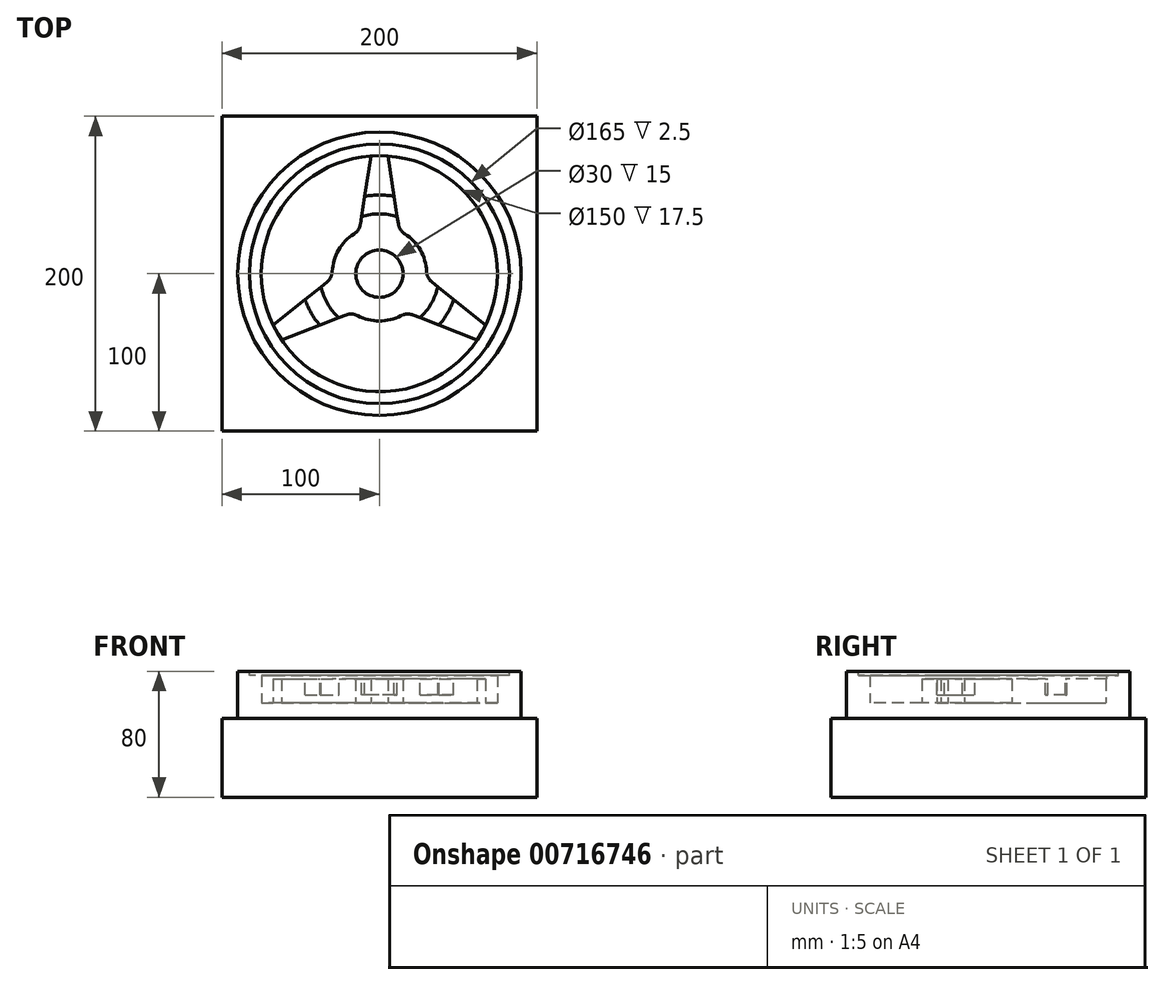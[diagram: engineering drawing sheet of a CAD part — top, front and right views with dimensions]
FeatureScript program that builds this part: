
annotation { "Feature Type Name" : "Feature", "Feature Type Description" : "" }
export const myFeature = defineFeature(function(context is Context, id is Id, definition is map)
    precondition{}
    {
        {
            var Q0;
            Q0=qCreatedBy(makeId("Top.planeOp"),FACE);
            var sketch = newSketch(context, id + "F0", { "sketchPlane" : qUnion([Q0])});
            skLineSegment(sketch, "E0.bottom", {"start": v(-100, 100) * mm, "end": v(100, 100) * mm});
            skLineSegment(sketch, "E0.top", {"start": v(-100, -100) * mm, "end": v(100, -100) * mm});
            skLineSegment(sketch, "E0.left", {"start": v(-100, 100) * mm, "end": v(-100, -100) * mm});
            skLineSegment(sketch, "E0.right", {"start": v(100, 100) * mm, "end": v(100, -100) * mm});
            skPoint(sketch, "E0.middle", {"position": v(0, 0) * mm});
            skCircle(sketch, "E1", {"center": v(0, 0) * mm, "radius": 90 * mm});
            skCircle(sketch, "E2", {"center": v(0, 0) * mm, "radius": 75 * mm});
            skCircle(sketch, "E3", {"center": v(0, 0) * mm, "radius": 30 * mm});
            skCircle(sketch, "E4", {"center": v(0, 0) * mm, "radius": 15 * mm});
            skLineSegment(sketch, "E5", {"start": v(0, 100) * mm, "end": v(0, -100) * mm, "construction": true});
            skLineSegment(sketch, "E6", {"start": v(-5.42, 74.8) * mm, "end": v(-12.73, 27.17) * mm});
            skLineSegment(sketch, "E7.MirrorCS", {"start": v(5.42, 74.8) * mm, "end": v(12.73, 27.17) * mm});
            skLineSegment(sketch, "E8.1.0", {"start": v(-67.5, -32.7) * mm, "end": v(-29.9, -2.56) * mm});
            skLineSegment(sketch, "E8.1.1", {"start": v(-62.07, -42.1) * mm, "end": v(-17.16, -24.6) * mm});
            skLineSegment(sketch, "E8.2.0", {"start": v(62.07, -42.1) * mm, "end": v(17.16, -24.6) * mm});
            skLineSegment(sketch, "E8.2.1", {"start": v(67.5, -32.7) * mm, "end": v(29.9, -2.56) * mm});
            skSolve(sketch);
        }
        {
            var Q0;
            Q0=makeQuery(id+"F0.imprint","IMPRINT",FACE,{"disambiguationData":[TD([[makeQuery(id+"F0.imprint","IMPRINT",EDGE,{"derivedFrom":sQuery(id+"F0.wireOp",EDGE,"E0.bottom")}),-1.0]])]});
            var Q1;
            Q1=makeQuery(id+"F0.imprint","IMPRINT",FACE,{"disambiguationData":[TD([[makeQuery(id+"F0.imprint","IMPRINT",EDGE,{"derivedFrom":sQuery(id+"F0.wireOp",EDGE,"E1")}),1.0]])]});
            var Q2;
            {var subQ0=sQuery(id+"F0.wireOp",EDGE,"E6");Q2=makeQuery(id+"F0.imprint","IMPRINT",FACE,{"disambiguationData":[TD([[makeQuery(id+"F0.imprint","IMPRINT",EDGE,{"derivedFrom":subQ0}),-1.0]])]});}
            var Q3;
            {var subQ0=sQuery(id+"F0.wireOp",EDGE,"fdc0faed-76a0-460e-8b43-f14472de8eec.1.0");Q3=makeQuery(id+"F0.imprint","IMPRINT",FACE,{"disambiguationData":[TD([[makeQuery(id+"F0.imprint","IMPRINT",EDGE,{"derivedFrom":subQ0}),-1.0]])]});}
            var Q4;
            {var subQ0=sQuery(id+"F0.wireOp",EDGE,"fdc0faed-76a0-460e-8b43-f14472de8eec.1.1");Q4=makeQuery(id+"F0.imprint","IMPRINT",FACE,{"disambiguationData":[TD([[makeQuery(id+"F0.imprint","IMPRINT",EDGE,{"derivedFrom":subQ0}),-1.0]])]});}
            var Q5;
            {var subQ0=sQuery(id+"F0.wireOp",EDGE,"fdc0faed-76a0-460e-8b43-f14472de8eec.2.0");Q5=makeQuery(id+"F0.imprint","IMPRINT",FACE,{"disambiguationData":[TD([[makeQuery(id+"F0.imprint","IMPRINT",EDGE,{"derivedFrom":subQ0}),-1.0]])]});}
            var Q6;
            Q6=makeQuery(id+"F0.imprint","IMPRINT",FACE,{"disambiguationData":[TD([[makeQuery(id+"F0.imprint","IMPRINT",EDGE,{"derivedFrom":sQuery(id+"F0.wireOp",EDGE,"E4")}),-1.0]])]});
            var Q7;
            Q7=makeQuery(id+"F0.imprint","IMPRINT",FACE,{"disambiguationData":[TD([[makeQuery(id+"F0.imprint","IMPRINT",EDGE,{"derivedFrom":sQuery(id+"F0.wireOp",EDGE,"E4")}),1.0]])]});
            var Q8;
            {var subQ0=sQuery(id+"F0.wireOp",EDGE,"fdc0faed-76a0-460e-8b43-f14472de8eec.3.0");Q8=makeQuery(id+"F0.imprint","IMPRINT",FACE,{"disambiguationData":[TD([[makeQuery(id+"F0.imprint","IMPRINT",EDGE,{"derivedFrom":subQ0}),-1.0]])]});}
            var Q9;
            {var subQ0=sQuery(id+"F0.wireOp",EDGE,"fdc0faed-76a0-460e-8b43-f14472de8eec.3.1");Q9=makeQuery(id+"F0.imprint","IMPRINT",FACE,{"disambiguationData":[TD([[makeQuery(id+"F0.imprint","IMPRINT",EDGE,{"derivedFrom":subQ0}),-1.0]])]});}
            var Q10;
            {var subQ0=sQuery(id+"F0.wireOp",EDGE,"E7.MirrorCS");Q10=makeQuery(id+"F0.imprint","IMPRINT",FACE,{"disambiguationData":[TD([[makeQuery(id+"F0.imprint","IMPRINT",EDGE,{"derivedFrom":subQ0}),1.0]])]});}
            var Q11;
            {var subQ0=sQuery(id+"F0.wireOp",EDGE,"fdc0faed-76a0-460e-8b43-f14472de8eec.4.0");Q11=makeQuery(id+"F0.imprint","IMPRINT",FACE,{"disambiguationData":[TD([[makeQuery(id+"F0.imprint","IMPRINT",EDGE,{"derivedFrom":subQ0}),-1.0]])]});}
            var Q12;
            {var subQ0=sQuery(id+"F0.wireOp",EDGE,"E6");Q12=makeQuery(id+"F0.imprint","IMPRINT",FACE,{"disambiguationData":[TD([[makeQuery(id+"F0.imprint","IMPRINT",EDGE,{"derivedFrom":subQ0}),1.0]])]});}
            var Q13;
            {var subQ0=sQuery(id+"F0.wireOp",EDGE,"fdc0faed-76a0-460e-8b43-f14472de8eec.2.1");Q13=makeQuery(id+"F0.imprint","IMPRINT",FACE,{"disambiguationData":[TD([[makeQuery(id+"F0.imprint","IMPRINT",EDGE,{"derivedFrom":subQ0}),-1.0]])]});}
            var Q14;
            {var subQ0=sQuery(id+"F0.wireOp",EDGE,"E8.1.0");Q14=makeQuery(id+"F0.imprint","IMPRINT",FACE,{"disambiguationData":[TD([[makeQuery(id+"F0.imprint","IMPRINT",EDGE,{"derivedFrom":subQ0}),-1.0]])]});}
            var Q15;
            {var subQ0=sQuery(id+"F0.wireOp",EDGE,"E8.1.1");Q15=makeQuery(id+"F0.imprint","IMPRINT",FACE,{"disambiguationData":[TD([[makeQuery(id+"F0.imprint","IMPRINT",EDGE,{"derivedFrom":subQ0}),-1.0]])]});}
            var Q16;
            {var subQ0=sQuery(id+"F0.wireOp",EDGE,"E8.2.0");Q16=makeQuery(id+"F0.imprint","IMPRINT",FACE,{"disambiguationData":[TD([[makeQuery(id+"F0.imprint","IMPRINT",EDGE,{"derivedFrom":subQ0}),-1.0]])]});}
            extrude(context, id + "F1", {"entities" : qUnion([Q0, Q1, Q2, Q3, Q4, Q5, Q6, Q7, Q8, Q9, Q10, Q11, Q12, Q13, Q14, Q15, Q16]), "depth" : 65 * mm, "offsetDistance" : 25 * mm});
        }
        {
            var Q0;
            Q0=makeQuery(id+"F0.imprint","IMPRINT",FACE,{"disambiguationData":[TD([[makeQuery(id+"F0.imprint","IMPRINT",EDGE,{"derivedFrom":sQuery(id+"F0.wireOp",EDGE,"E1")}),1.0]])]});
            extrude(context, id + "F2", {"entities" : qUnion([Q0]), "operationType" : NewBodyOperationType.ADD, "depth" : 80 * mm, "offsetDistance" : 25 * mm});
        }
        {
            var Q0;
            {var subQ0=sQuery(id+"F0.wireOp",EDGE,"fdc0faed-76a0-460e-8b43-f14472de8eec.3.0");Q0=makeQuery(id+"F0.imprint","IMPRINT",FACE,{"disambiguationData":[TD([[makeQuery(id+"F0.imprint","IMPRINT",EDGE,{"derivedFrom":subQ0}),-1.0]])]});}
            var Q1;
            Q1=makeQuery(id+"F0.imprint","IMPRINT",FACE,{"disambiguationData":[TD([[makeQuery(id+"F0.imprint","IMPRINT",EDGE,{"derivedFrom":sQuery(id+"F0.wireOp",EDGE,"E4")}),-1.0]])]});
            var Q2;
            {var subQ0=sQuery(id+"F0.wireOp",EDGE,"fdc0faed-76a0-460e-8b43-f14472de8eec.4.0");Q2=makeQuery(id+"F0.imprint","IMPRINT",FACE,{"disambiguationData":[TD([[makeQuery(id+"F0.imprint","IMPRINT",EDGE,{"derivedFrom":subQ0}),-1.0]])]});}
            var Q3;
            {var subQ0=sQuery(id+"F0.wireOp",EDGE,"E6");Q3=makeQuery(id+"F0.imprint","IMPRINT",FACE,{"disambiguationData":[TD([[makeQuery(id+"F0.imprint","IMPRINT",EDGE,{"derivedFrom":subQ0}),1.0]])]});}
            var Q4;
            {var subQ0=sQuery(id+"F0.wireOp",EDGE,"fdc0faed-76a0-460e-8b43-f14472de8eec.1.0");Q4=makeQuery(id+"F0.imprint","IMPRINT",FACE,{"disambiguationData":[TD([[makeQuery(id+"F0.imprint","IMPRINT",EDGE,{"derivedFrom":subQ0}),-1.0]])]});}
            var Q5;
            {var subQ0=sQuery(id+"F0.wireOp",EDGE,"fdc0faed-76a0-460e-8b43-f14472de8eec.2.0");Q5=makeQuery(id+"F0.imprint","IMPRINT",FACE,{"disambiguationData":[TD([[makeQuery(id+"F0.imprint","IMPRINT",EDGE,{"derivedFrom":subQ0}),-1.0]])]});}
            var Q6;
            {var subQ0=sQuery(id+"F0.wireOp",EDGE,"E8.1.0");Q6=makeQuery(id+"F0.imprint","IMPRINT",FACE,{"disambiguationData":[TD([[makeQuery(id+"F0.imprint","IMPRINT",EDGE,{"derivedFrom":subQ0}),-1.0]])]});}
            var Q7;
            {var subQ0=sQuery(id+"F0.wireOp",EDGE,"E8.2.0");Q7=makeQuery(id+"F0.imprint","IMPRINT",FACE,{"disambiguationData":[TD([[makeQuery(id+"F0.imprint","IMPRINT",EDGE,{"derivedFrom":subQ0}),-1.0]])]});}
            extrude(context, id + "F3", {"entities" : qUnion([Q0, Q1, Q2, Q3, Q4, Q5, Q6, Q7]), "operationType" : NewBodyOperationType.ADD, "depth" : 70 * mm, "offsetDistance" : 25 * mm});
        }
        {
            var Q0;
            Q0=makeQuery(id+"F0.imprint","IMPRINT",FACE,{"disambiguationData":[TD([[makeQuery(id+"F0.imprint","IMPRINT",EDGE,{"derivedFrom":sQuery(id+"F0.wireOp",EDGE,"E4")}),-1.0]])]});
            extrude(context, id + "F4", {"entities" : qUnion([Q0]), "operationType" : NewBodyOperationType.ADD, "depth" : 75 * mm, "offsetDistance" : 25 * mm});
        }
        {
            var Q0;
            Q0=makeQuery(id+"F3.opExtrude","SWEPT_EDGE",EDGE,{"disambiguationData":[OSD([sQuery(id+"F0.wireOp",EDGE,"E3"),sQuery(id+"F0.wireOp",EDGE,"fdc0faed-76a0-460e-8b43-f14472de8eec.1.0")])]});
            var Q1;
            Q1=makeQuery(id+"F3.opExtrude","SWEPT_EDGE",EDGE,{"disambiguationData":[OSD([sQuery(id+"F0.wireOp",EDGE,"E3"),sQuery(id+"F0.wireOp",EDGE,"E6")])]});
            var Q2;
            Q2=makeQuery(id+"F3.opExtrude","SWEPT_EDGE",EDGE,{"disambiguationData":[OSD([sQuery(id+"F0.wireOp",EDGE,"E2"),sQuery(id+"F0.wireOp",EDGE,"E6")])]});
            var Q3;
            Q3=makeQuery(id+"F3.opExtrude","SWEPT_EDGE",EDGE,{"disambiguationData":[OSD([sQuery(id+"F0.wireOp",EDGE,"E2"),sQuery(id+"F0.wireOp",EDGE,"fdc0faed-76a0-460e-8b43-f14472de8eec.1.0")])]});
            var Q4;
            Q4=makeQuery(id+"F3.opExtrude","SWEPT_EDGE",EDGE,{"disambiguationData":[OSD([sQuery(id+"F0.wireOp",EDGE,"E2"),sQuery(id+"F0.wireOp",EDGE,"E7.MirrorCS")])]});
            var Q5;
            Q5=makeQuery(id+"F3.opExtrude","SWEPT_EDGE",EDGE,{"disambiguationData":[OSD([sQuery(id+"F0.wireOp",EDGE,"E2"),sQuery(id+"F0.wireOp",EDGE,"fdc0faed-76a0-460e-8b43-f14472de8eec.4.1")])]});
            var Q6;
            Q6=makeQuery(id+"F3.opExtrude","SWEPT_EDGE",EDGE,{"disambiguationData":[OSD([sQuery(id+"F0.wireOp",EDGE,"E3"),sQuery(id+"F0.wireOp",EDGE,"E7.MirrorCS")])]});
            var Q7;
            Q7=makeQuery(id+"F3.opExtrude","SWEPT_EDGE",EDGE,{"disambiguationData":[OSD([sQuery(id+"F0.wireOp",EDGE,"E3"),sQuery(id+"F0.wireOp",EDGE,"fdc0faed-76a0-460e-8b43-f14472de8eec.4.1")])]});
            var Q8;
            Q8=makeQuery(id+"F3.opExtrude","SWEPT_EDGE",EDGE,{"disambiguationData":[OSD([sQuery(id+"F0.wireOp",EDGE,"E3"),sQuery(id+"F0.wireOp",EDGE,"fdc0faed-76a0-460e-8b43-f14472de8eec.4.0")])]});
            var Q9;
            Q9=makeQuery(id+"F3.opExtrude","SWEPT_EDGE",EDGE,{"disambiguationData":[OSD([sQuery(id+"F0.wireOp",EDGE,"E3"),sQuery(id+"F0.wireOp",EDGE,"fdc0faed-76a0-460e-8b43-f14472de8eec.3.1")])]});
            var Q10;
            Q10=makeQuery(id+"F3.opExtrude","SWEPT_EDGE",EDGE,{"disambiguationData":[OSD([sQuery(id+"F0.wireOp",EDGE,"E2"),sQuery(id+"F0.wireOp",EDGE,"fdc0faed-76a0-460e-8b43-f14472de8eec.3.1")])]});
            var Q11;
            Q11=makeQuery(id+"F3.opExtrude","SWEPT_EDGE",EDGE,{"disambiguationData":[OSD([sQuery(id+"F0.wireOp",EDGE,"E2"),sQuery(id+"F0.wireOp",EDGE,"fdc0faed-76a0-460e-8b43-f14472de8eec.3.0")])]});
            var Q12;
            Q12=makeQuery(id+"F3.opExtrude","SWEPT_EDGE",EDGE,{"disambiguationData":[OSD([sQuery(id+"F0.wireOp",EDGE,"E3"),sQuery(id+"F0.wireOp",EDGE,"fdc0faed-76a0-460e-8b43-f14472de8eec.2.1")])]});
            var Q13;
            Q13=makeQuery(id+"F3.opExtrude","SWEPT_EDGE",EDGE,{"disambiguationData":[OSD([sQuery(id+"F0.wireOp",EDGE,"E3"),sQuery(id+"F0.wireOp",EDGE,"fdc0faed-76a0-460e-8b43-f14472de8eec.3.0")])]});
            var Q14;
            Q14=makeQuery(id+"F3.opExtrude","SWEPT_EDGE",EDGE,{"disambiguationData":[OSD([sQuery(id+"F0.wireOp",EDGE,"E2"),sQuery(id+"F0.wireOp",EDGE,"fdc0faed-76a0-460e-8b43-f14472de8eec.2.1")])]});
            var Q15;
            Q15=makeQuery(id+"F3.opExtrude","SWEPT_EDGE",EDGE,{"disambiguationData":[OSD([sQuery(id+"F0.wireOp",EDGE,"E2"),sQuery(id+"F0.wireOp",EDGE,"fdc0faed-76a0-460e-8b43-f14472de8eec.2.0")])]});
            var Q16;
            Q16=makeQuery(id+"F3.opExtrude","SWEPT_EDGE",EDGE,{"disambiguationData":[OSD([sQuery(id+"F0.wireOp",EDGE,"E3"),sQuery(id+"F0.wireOp",EDGE,"fdc0faed-76a0-460e-8b43-f14472de8eec.2.0")])]});
            var Q17;
            Q17=makeQuery(id+"F3.opExtrude","SWEPT_EDGE",EDGE,{"disambiguationData":[OSD([sQuery(id+"F0.wireOp",EDGE,"E3"),sQuery(id+"F0.wireOp",EDGE,"fdc0faed-76a0-460e-8b43-f14472de8eec.1.1")])]});
            var Q18;
            Q18=makeQuery(id+"F3.opExtrude","SWEPT_EDGE",EDGE,{"disambiguationData":[OSD([sQuery(id+"F0.wireOp",EDGE,"E2"),sQuery(id+"F0.wireOp",EDGE,"fdc0faed-76a0-460e-8b43-f14472de8eec.1.1")])]});
            var Q19;
            Q19=makeQuery(id+"F3.opExtrude","SWEPT_EDGE",EDGE,{"disambiguationData":[OSD([sQuery(id+"F0.wireOp",EDGE,"E2"),sQuery(id+"F0.wireOp",EDGE,"fdc0faed-76a0-460e-8b43-f14472de8eec.4.0")])]});
            fillet(context, id + "F5", {"entities" : qUnion([Q0, Q1, Q2, Q3, Q4, Q5, Q6, Q7, Q8, Q9, Q10, Q11, Q12, Q13, Q14, Q15, Q16, Q17, Q18, Q19]), "radius" : 9.1 * mm, "tangentPropagation" : true, "allowEdgeOverflow" : false});
        }
        {
            var Q0;
            {var subQ0=sQuery(id+"F0.wireOp",EDGE,"fdc0faed-76a0-460e-8b43-f14472de8eec.1.1");var subQ1=sQuery(id+"F0.wireOp",EDGE,"E3");var subQ2=sQuery(id+"F0.wireOp",EDGE,"fdc0faed-76a0-460e-8b43-f14472de8eec.2.0");var subQ3=sQuery(id+"F0.wireOp",EDGE,"fdc0faed-76a0-460e-8b43-f14472de8eec.3.1");var subQ4=sQuery(id+"F0.wireOp",EDGE,"E6");var subQ5=sQuery(id+"F0.wireOp",EDGE,"fdc0faed-76a0-460e-8b43-f14472de8eec.1.0");var subQ6=sQuery(id+"F0.wireOp",EDGE,"fdc0faed-76a0-460e-8b43-f14472de8eec.3.0");var subQ7=sQuery(id+"F0.wireOp",EDGE,"E7.MirrorCS");var subQ8=sQuery(id+"F0.wireOp",EDGE,"fdc0faed-76a0-460e-8b43-f14472de8eec.4.1");var subQ9=sQuery(id+"F0.wireOp",EDGE,"E2");var subQ10=sQuery(id+"F0.wireOp",EDGE,"fdc0faed-76a0-460e-8b43-f14472de8eec.2.1");var subQ11=sQuery(id+"F0.wireOp",EDGE,"fdc0faed-76a0-460e-8b43-f14472de8eec.4.0");Q0=makeQuery(id+"F4.boolean.opBoolean","SPLIT",FACE,{"disambiguationData":[TD([makeQuery(id+"F3.opExtrude","SWEPT_FACE",FACE,{"disambiguationData":[OSD([subQ6])]})])],"derivedFrom":makeQuery(id+"F3.opExtrude","CAP_FACE",FACE,{"disambiguationData":[OSD([subQ9,subQ1,sQuery(id+"F0.wireOp",EDGE,"E4"),subQ4,subQ7,subQ5,subQ0,subQ2,subQ10,subQ6,subQ3,subQ11,subQ8])],"isStart":false})});}
            var Q1;
            {var subQ0=sQuery(id+"F0.wireOp",EDGE,"fdc0faed-76a0-460e-8b43-f14472de8eec.1.1");var subQ1=sQuery(id+"F0.wireOp",EDGE,"E3");var subQ2=sQuery(id+"F0.wireOp",EDGE,"fdc0faed-76a0-460e-8b43-f14472de8eec.2.0");var subQ3=sQuery(id+"F0.wireOp",EDGE,"E6");var subQ4=sQuery(id+"F0.wireOp",EDGE,"fdc0faed-76a0-460e-8b43-f14472de8eec.1.0");var subQ5=sQuery(id+"F0.wireOp",EDGE,"E7.MirrorCS");var subQ6=sQuery(id+"F0.wireOp",EDGE,"fdc0faed-76a0-460e-8b43-f14472de8eec.4.1");var subQ7=sQuery(id+"F0.wireOp",EDGE,"fdc0faed-76a0-460e-8b43-f14472de8eec.2.1");var subQ8=sQuery(id+"F0.wireOp",EDGE,"E2");var subQ9=sQuery(id+"F0.wireOp",EDGE,"fdc0faed-76a0-460e-8b43-f14472de8eec.3.0");var subQ10=sQuery(id+"F0.wireOp",EDGE,"fdc0faed-76a0-460e-8b43-f14472de8eec.3.1");var subQ11=sQuery(id+"F0.wireOp",EDGE,"fdc0faed-76a0-460e-8b43-f14472de8eec.4.0");Q1=makeQuery(id+"F4.boolean.opBoolean","SPLIT",FACE,{"disambiguationData":[TD([makeQuery(id+"F3.opExtrude","SWEPT_FACE",FACE,{"disambiguationData":[OSD([subQ2])]})])],"derivedFrom":makeQuery(id+"F3.opExtrude","CAP_FACE",FACE,{"disambiguationData":[OSD([subQ8,subQ1,sQuery(id+"F0.wireOp",EDGE,"E4"),subQ3,subQ5,subQ4,subQ0,subQ2,subQ7,subQ9,subQ10,subQ11,subQ6])],"isStart":false})});}
            var Q2;
            {var subQ0=sQuery(id+"F0.wireOp",EDGE,"fdc0faed-76a0-460e-8b43-f14472de8eec.1.1");var subQ1=sQuery(id+"F0.wireOp",EDGE,"E3");var subQ2=sQuery(id+"F0.wireOp",EDGE,"fdc0faed-76a0-460e-8b43-f14472de8eec.2.0");var subQ3=sQuery(id+"F0.wireOp",EDGE,"E6");var subQ4=sQuery(id+"F0.wireOp",EDGE,"fdc0faed-76a0-460e-8b43-f14472de8eec.1.0");var subQ5=sQuery(id+"F0.wireOp",EDGE,"E7.MirrorCS");var subQ6=sQuery(id+"F0.wireOp",EDGE,"fdc0faed-76a0-460e-8b43-f14472de8eec.4.1");var subQ7=sQuery(id+"F0.wireOp",EDGE,"E2");var subQ8=sQuery(id+"F0.wireOp",EDGE,"fdc0faed-76a0-460e-8b43-f14472de8eec.2.1");var subQ9=sQuery(id+"F0.wireOp",EDGE,"fdc0faed-76a0-460e-8b43-f14472de8eec.3.0");var subQ10=sQuery(id+"F0.wireOp",EDGE,"fdc0faed-76a0-460e-8b43-f14472de8eec.3.1");var subQ11=sQuery(id+"F0.wireOp",EDGE,"fdc0faed-76a0-460e-8b43-f14472de8eec.4.0");Q2=makeQuery(id+"F4.boolean.opBoolean","SPLIT",FACE,{"disambiguationData":[TD([makeQuery(id+"F3.opExtrude","SWEPT_FACE",FACE,{"disambiguationData":[OSD([subQ4])]})])],"derivedFrom":makeQuery(id+"F3.opExtrude","CAP_FACE",FACE,{"disambiguationData":[OSD([subQ7,subQ1,sQuery(id+"F0.wireOp",EDGE,"E4"),subQ3,subQ5,subQ4,subQ0,subQ2,subQ8,subQ9,subQ10,subQ11,subQ6])],"isStart":false})});}
            var Q3;
            {var subQ0=sQuery(id+"F0.wireOp",EDGE,"fdc0faed-76a0-460e-8b43-f14472de8eec.1.1");var subQ1=sQuery(id+"F0.wireOp",EDGE,"E3");var subQ2=sQuery(id+"F0.wireOp",EDGE,"fdc0faed-76a0-460e-8b43-f14472de8eec.2.0");var subQ3=sQuery(id+"F0.wireOp",EDGE,"E6");var subQ4=sQuery(id+"F0.wireOp",EDGE,"fdc0faed-76a0-460e-8b43-f14472de8eec.1.0");var subQ5=sQuery(id+"F0.wireOp",EDGE,"E7.MirrorCS");var subQ6=sQuery(id+"F0.wireOp",EDGE,"fdc0faed-76a0-460e-8b43-f14472de8eec.4.1");var subQ7=sQuery(id+"F0.wireOp",EDGE,"E2");var subQ8=sQuery(id+"F0.wireOp",EDGE,"fdc0faed-76a0-460e-8b43-f14472de8eec.2.1");var subQ9=sQuery(id+"F0.wireOp",EDGE,"fdc0faed-76a0-460e-8b43-f14472de8eec.3.0");var subQ10=sQuery(id+"F0.wireOp",EDGE,"fdc0faed-76a0-460e-8b43-f14472de8eec.3.1");var subQ11=sQuery(id+"F0.wireOp",EDGE,"fdc0faed-76a0-460e-8b43-f14472de8eec.4.0");Q3=makeQuery(id+"F4.boolean.opBoolean","SPLIT",FACE,{"disambiguationData":[TD([makeQuery(id+"F3.opExtrude","SWEPT_FACE",FACE,{"disambiguationData":[OSD([subQ3])]})])],"derivedFrom":makeQuery(id+"F3.opExtrude","CAP_FACE",FACE,{"disambiguationData":[OSD([subQ7,subQ1,sQuery(id+"F0.wireOp",EDGE,"E4"),subQ3,subQ5,subQ4,subQ0,subQ2,subQ8,subQ9,subQ10,subQ11,subQ6])],"isStart":false})});}
            var Q4;
            {var subQ0=sQuery(id+"F0.wireOp",EDGE,"fdc0faed-76a0-460e-8b43-f14472de8eec.1.1");var subQ1=sQuery(id+"F0.wireOp",EDGE,"E3");var subQ2=sQuery(id+"F0.wireOp",EDGE,"fdc0faed-76a0-460e-8b43-f14472de8eec.2.0");var subQ3=sQuery(id+"F0.wireOp",EDGE,"E6");var subQ4=sQuery(id+"F0.wireOp",EDGE,"fdc0faed-76a0-460e-8b43-f14472de8eec.1.0");var subQ5=sQuery(id+"F0.wireOp",EDGE,"E7.MirrorCS");var subQ6=sQuery(id+"F0.wireOp",EDGE,"fdc0faed-76a0-460e-8b43-f14472de8eec.4.1");var subQ7=sQuery(id+"F0.wireOp",EDGE,"E2");var subQ8=sQuery(id+"F0.wireOp",EDGE,"fdc0faed-76a0-460e-8b43-f14472de8eec.2.1");var subQ9=sQuery(id+"F0.wireOp",EDGE,"fdc0faed-76a0-460e-8b43-f14472de8eec.3.0");var subQ10=sQuery(id+"F0.wireOp",EDGE,"fdc0faed-76a0-460e-8b43-f14472de8eec.4.0");var subQ11=sQuery(id+"F0.wireOp",EDGE,"fdc0faed-76a0-460e-8b43-f14472de8eec.3.1");Q4=makeQuery(id+"F4.boolean.opBoolean","SPLIT",FACE,{"disambiguationData":[TD([makeQuery(id+"F3.opExtrude","SWEPT_FACE",FACE,{"disambiguationData":[OSD([subQ10])]})])],"derivedFrom":makeQuery(id+"F3.opExtrude","CAP_FACE",FACE,{"disambiguationData":[OSD([subQ7,subQ1,sQuery(id+"F0.wireOp",EDGE,"E4"),subQ3,subQ5,subQ4,subQ0,subQ2,subQ8,subQ9,subQ11,subQ10,subQ6])],"isStart":false})});}
            var Q5;
            {var subQ0=sQuery(id+"F0.wireOp",EDGE,"E7.MirrorCS");var subQ1=sQuery(id+"F0.wireOp",EDGE,"E3");var subQ2=sQuery(id+"F0.wireOp",EDGE,"E8.2.1");var subQ3=sQuery(id+"F0.wireOp",EDGE,"E6");var subQ4=sQuery(id+"F0.wireOp",EDGE,"E8.1.0");var subQ5=sQuery(id+"F0.wireOp",EDGE,"E8.1.1");var subQ6=sQuery(id+"F0.wireOp",EDGE,"E8.2.0");var subQ7=sQuery(id+"F0.wireOp",EDGE,"E2");Q5=makeQuery(id+"F4.boolean.opBoolean","SPLIT",FACE,{"disambiguationData":[TD([makeQuery(id+"F3.opExtrude","SWEPT_FACE",FACE,{"disambiguationData":[OSD([subQ6])]})])],"derivedFrom":makeQuery(id+"F3.opExtrude","CAP_FACE",FACE,{"disambiguationData":[OSD([subQ7,subQ1,sQuery(id+"F0.wireOp",EDGE,"E4"),subQ3,subQ0,subQ4,subQ5,subQ6,subQ2])],"isStart":false})});}
            var Q6;
            {var subQ0=sQuery(id+"F0.wireOp",EDGE,"E7.MirrorCS");var subQ1=sQuery(id+"F0.wireOp",EDGE,"E3");var subQ2=sQuery(id+"F0.wireOp",EDGE,"E8.2.1");var subQ3=sQuery(id+"F0.wireOp",EDGE,"E6");var subQ4=sQuery(id+"F0.wireOp",EDGE,"E8.1.0");var subQ5=sQuery(id+"F0.wireOp",EDGE,"E8.1.1");var subQ6=sQuery(id+"F0.wireOp",EDGE,"E8.2.0");var subQ7=sQuery(id+"F0.wireOp",EDGE,"E2");Q6=makeQuery(id+"F4.boolean.opBoolean","SPLIT",FACE,{"disambiguationData":[TD([makeQuery(id+"F3.opExtrude","SWEPT_FACE",FACE,{"disambiguationData":[OSD([subQ4])]})])],"derivedFrom":makeQuery(id+"F3.opExtrude","CAP_FACE",FACE,{"disambiguationData":[OSD([subQ7,subQ1,sQuery(id+"F0.wireOp",EDGE,"E4"),subQ3,subQ0,subQ4,subQ5,subQ6,subQ2])],"isStart":false})});}
            var Q7;
            Q7=makeQuery(id+"F4.opExtrude","CAP_FACE",FACE,{"disambiguationData":[OSD([sQuery(id+"F0.wireOp",EDGE,"E3"),sQuery(id+"F0.wireOp",EDGE,"E4")])],"isStart":false});
            extrude(context, id + "F6", {"entities" : qUnion([Q0, Q1, Q2, Q3, Q4, Q5, Q6]), "operationType" : NewBodyOperationType.ADD, "endBound" : BoundingType.UP_TO_SURFACE, "depth" : 25 * mm, "endBoundEntityFace" : qUnion([Q7]), "offsetDistance" : 25 * mm});
        }
        {
            var Q0;
            Q0=makeQuery(id+"F2.opExtrude","CAP_FACE",FACE,{"disambiguationData":[OSD([sQuery(id+"F0.wireOp",EDGE,"E1"),sQuery(id+"F0.wireOp",EDGE,"E2")])],"isStart":false});
            var sketch = newSketch(context, id + "F7", { "sketchPlane" : qUnion([Q0])});
            skCircle(sketch, "E9.0", {"center": v(0, 0) * mm, "radius": 90 * mm});
            skCircle(sketch, "E10", {"center": v(0, 0) * mm, "radius": 82.5 * mm});
            skSolve(sketch);
        }
        {
            var Q0;
            Q0=makeQuery(id+"F7.imprint","IMPRINT",FACE,{"disambiguationData":[TD([[makeQuery(id+"F7.imprint","IMPRINT",EDGE,{"derivedFrom":sQuery(id+"F7.wireOp",EDGE,"E10")}),1.0]])]});
            extrude(context, id + "F8", {"entities" : qUnion([Q0]), "operationType" : NewBodyOperationType.REMOVE, "oppositeDirection" : true, "depth" : 2.5 * mm, "offsetDistance" : 25 * mm});
        }
        {
            var Q0;
            {var subQ0=makeQuery(id+"F2.opExtrude","SWEPT_FACE",FACE,{"disambiguationData":[OSD([sQuery(id+"F0.wireOp",EDGE,"E2")])]});var subQ1=sQuery(id+"F0.wireOp",EDGE,"E6");Q0=makeQuery(id+"F3.boolean.opBoolean","SPLIT",FACE,{"disambiguationData":[TD([makeQuery(id+"F3.opExtrude","SWEPT_FACE",FACE,{"disambiguationData":[OSD([subQ1])]})])],"derivedFrom":makeQuery(id+"F2.boolean.opBoolean","SPLIT",FACE,{"disambiguationData":[TD([subQ0])],"derivedFrom":makeQuery(id+"F1.opExtrude","CAP_FACE",FACE,{"disambiguationData":[OSD([sQuery(id+"F0.wireOp",EDGE,"E0.bottom"),sQuery(id+"F0.wireOp",EDGE,"E0.top"),sQuery(id+"F0.wireOp",EDGE,"E0.left"),sQuery(id+"F0.wireOp",EDGE,"E0.right")])],"isStart":false})})});}
            var Q1;
            {var subQ0=makeQuery(id+"F2.opExtrude","SWEPT_FACE",FACE,{"disambiguationData":[OSD([sQuery(id+"F0.wireOp",EDGE,"E2")])]});var subQ1=sQuery(id+"F0.wireOp",EDGE,"E7.MirrorCS");Q1=makeQuery(id+"F3.boolean.opBoolean","SPLIT",FACE,{"disambiguationData":[TD([makeQuery(id+"F3.opExtrude","SWEPT_FACE",FACE,{"disambiguationData":[OSD([subQ1])]})])],"derivedFrom":makeQuery(id+"F2.boolean.opBoolean","SPLIT",FACE,{"disambiguationData":[TD([subQ0])],"derivedFrom":makeQuery(id+"F1.opExtrude","CAP_FACE",FACE,{"disambiguationData":[OSD([sQuery(id+"F0.wireOp",EDGE,"E0.bottom"),sQuery(id+"F0.wireOp",EDGE,"E0.top"),sQuery(id+"F0.wireOp",EDGE,"E0.left"),sQuery(id+"F0.wireOp",EDGE,"E0.right")])],"isStart":false})})});}
            var Q2;
            {var subQ0=makeQuery(id+"F2.opExtrude","SWEPT_FACE",FACE,{"disambiguationData":[OSD([sQuery(id+"F0.wireOp",EDGE,"E2")])]});var subQ1=sQuery(id+"F0.wireOp",EDGE,"fdc0faed-76a0-460e-8b43-f14472de8eec.1.1");Q2=makeQuery(id+"F3.boolean.opBoolean","SPLIT",FACE,{"disambiguationData":[TD([makeQuery(id+"F3.opExtrude","SWEPT_FACE",FACE,{"disambiguationData":[OSD([subQ1])]})])],"derivedFrom":makeQuery(id+"F2.boolean.opBoolean","SPLIT",FACE,{"disambiguationData":[TD([subQ0])],"derivedFrom":makeQuery(id+"F1.opExtrude","CAP_FACE",FACE,{"disambiguationData":[OSD([sQuery(id+"F0.wireOp",EDGE,"E0.bottom"),sQuery(id+"F0.wireOp",EDGE,"E0.top"),sQuery(id+"F0.wireOp",EDGE,"E0.left"),sQuery(id+"F0.wireOp",EDGE,"E0.right")])],"isStart":false})})});}
            var Q3;
            {var subQ0=makeQuery(id+"F2.opExtrude","SWEPT_FACE",FACE,{"disambiguationData":[OSD([sQuery(id+"F0.wireOp",EDGE,"E2")])]});var subQ1=sQuery(id+"F0.wireOp",EDGE,"fdc0faed-76a0-460e-8b43-f14472de8eec.3.1");Q3=makeQuery(id+"F3.boolean.opBoolean","SPLIT",FACE,{"disambiguationData":[TD([makeQuery(id+"F3.opExtrude","SWEPT_FACE",FACE,{"disambiguationData":[OSD([subQ1])]})])],"derivedFrom":makeQuery(id+"F2.boolean.opBoolean","SPLIT",FACE,{"disambiguationData":[TD([subQ0])],"derivedFrom":makeQuery(id+"F1.opExtrude","CAP_FACE",FACE,{"disambiguationData":[OSD([sQuery(id+"F0.wireOp",EDGE,"E0.bottom"),sQuery(id+"F0.wireOp",EDGE,"E0.top"),sQuery(id+"F0.wireOp",EDGE,"E0.left"),sQuery(id+"F0.wireOp",EDGE,"E0.right")])],"isStart":false})})});}
            var Q4;
            {var subQ0=makeQuery(id+"F2.opExtrude","SWEPT_FACE",FACE,{"disambiguationData":[OSD([sQuery(id+"F0.wireOp",EDGE,"E2")])]});var subQ1=sQuery(id+"F0.wireOp",EDGE,"fdc0faed-76a0-460e-8b43-f14472de8eec.2.1");Q4=makeQuery(id+"F3.boolean.opBoolean","SPLIT",FACE,{"disambiguationData":[TD([makeQuery(id+"F3.opExtrude","SWEPT_FACE",FACE,{"disambiguationData":[OSD([subQ1])]})])],"derivedFrom":makeQuery(id+"F2.boolean.opBoolean","SPLIT",FACE,{"disambiguationData":[TD([subQ0])],"derivedFrom":makeQuery(id+"F1.opExtrude","CAP_FACE",FACE,{"disambiguationData":[OSD([sQuery(id+"F0.wireOp",EDGE,"E0.bottom"),sQuery(id+"F0.wireOp",EDGE,"E0.top"),sQuery(id+"F0.wireOp",EDGE,"E0.left"),sQuery(id+"F0.wireOp",EDGE,"E0.right")])],"isStart":false})})});}
            var Q5;
            Q5=makeQuery(id+"F3.boolean.opBoolean","SPLIT",FACE,{"disambiguationData":[TD([makeQuery(id+"F3.opExtrude","SWEPT_FACE",FACE,{"disambiguationData":[OSD([sQuery(id+"F0.wireOp",EDGE,"E4")])]})])],"derivedFrom":makeQuery(id+"F2.boolean.opBoolean","SPLIT",FACE,{"disambiguationData":[TD([makeQuery(id+"F2.opExtrude","SWEPT_FACE",FACE,{"disambiguationData":[OSD([sQuery(id+"F0.wireOp",EDGE,"E2")])]})])],"derivedFrom":makeQuery(id+"F1.opExtrude","CAP_FACE",FACE,{"disambiguationData":[OSD([sQuery(id+"F0.wireOp",EDGE,"E0.bottom"),sQuery(id+"F0.wireOp",EDGE,"E0.top"),sQuery(id+"F0.wireOp",EDGE,"E0.left"),sQuery(id+"F0.wireOp",EDGE,"E0.right")])],"isStart":false})})});
            var Q6;
            {var subQ0=makeQuery(id+"F2.opExtrude","SWEPT_FACE",FACE,{"disambiguationData":[OSD([sQuery(id+"F0.wireOp",EDGE,"E2")])]});var subQ1=sQuery(id+"F0.wireOp",EDGE,"E8.1.1");Q6=makeQuery(id+"F3.boolean.opBoolean","SPLIT",FACE,{"disambiguationData":[TD([makeQuery(id+"F3.opExtrude","SWEPT_FACE",FACE,{"disambiguationData":[OSD([subQ1])]})])],"derivedFrom":makeQuery(id+"F2.boolean.opBoolean","SPLIT",FACE,{"disambiguationData":[TD([subQ0])],"derivedFrom":makeQuery(id+"F1.opExtrude","CAP_FACE",FACE,{"disambiguationData":[OSD([sQuery(id+"F0.wireOp",EDGE,"E0.bottom"),sQuery(id+"F0.wireOp",EDGE,"E0.top"),sQuery(id+"F0.wireOp",EDGE,"E0.left"),sQuery(id+"F0.wireOp",EDGE,"E0.right")])],"isStart":false})})});}
            extrude(context, id + "F9", {"entities" : qUnion([Q0, Q1, Q2, Q3, Q4, Q5, Q6]), "operationType" : NewBodyOperationType.REMOVE, "oppositeDirection" : true, "depth" : 5 * mm, "offsetDistance" : 25 * mm});
        }
        {
            var Q0;
            {var subQ0=sQuery(id+"F0.wireOp",EDGE,"E0.left");var subQ1=sQuery(id+"F0.wireOp",EDGE,"E0.top");var subQ2=sQuery(id+"F0.wireOp",EDGE,"E0.right");var subQ3=sQuery(id+"F0.wireOp",EDGE,"E0.bottom");Q0=makeQuery(id+"F2.boolean.opBoolean","SPLIT",FACE,{"disambiguationData":[TD([makeQuery(id+"F1.opExtrude","SWEPT_FACE",FACE,{"disambiguationData":[OSD([subQ3])]})])],"derivedFrom":makeQuery(id+"F1.opExtrude","CAP_FACE",FACE,{"disambiguationData":[OSD([subQ3,subQ1,subQ0,subQ2])],"isStart":false})});}
            extrude(context, id + "F10", {"entities" : qUnion([Q0]), "operationType" : NewBodyOperationType.REMOVE, "oppositeDirection" : true, "depth" : 15 * mm, "offsetDistance" : 25 * mm});
        }
        {
            var Q0;
            {var subQ0=sQuery(id+"F0.wireOp",EDGE,"E7.MirrorCS");var subQ1=sQuery(id+"F0.wireOp",EDGE,"E3");var subQ2=sQuery(id+"F0.wireOp",EDGE,"E8.2.1");var subQ4=sQuery(id+"F0.wireOp",EDGE,"E6");var subQ5=sQuery(id+"F0.wireOp",EDGE,"E8.1.0");var subQ7=sQuery(id+"F0.wireOp",EDGE,"E8.1.1");var subQ8=sQuery(id+"F0.wireOp",EDGE,"E8.2.0");var subQ10=sQuery(id+"F0.wireOp",EDGE,"E2");var subQ13=sQuery(id+"F0.wireOp",EDGE,"E4");var subQ14=makeQuery(id+"F3.opExtrude","CAP_FACE",FACE,{"disambiguationData":[OSD([subQ10,subQ1,subQ13,subQ4,subQ0,subQ5,subQ7,subQ8,subQ2])],"isStart":false});Q0=makeQuery(id+"F6.boolean.opBoolean","MERGE",FACE,{"derivedFrom":[makeQuery(id+"F4.opExtrude","CAP_FACE",FACE,{"disambiguationData":[OSD([subQ1,subQ13])],"isStart":false}),makeQuery(id+"F6.opExtrude","CAP_FACE",FACE,{"disambiguationData":[OSD([subQ10,subQ1,subQ13,subQ4,subQ0,subQ5,subQ7,subQ8,subQ2]),TDD([makeQuery(id+"F4.boolean.opBoolean","SPLIT",FACE,{"disambiguationData":[TD([makeQuery(id+"F3.opExtrude","SWEPT_FACE",FACE,{"disambiguationData":[OSD([subQ4])]})])],"derivedFrom":subQ14})])],"isStart":false}),makeQuery(id+"F6.opExtrude","CAP_FACE",FACE,{"disambiguationData":[OSD([subQ10,subQ1,subQ13,subQ4,subQ0,subQ5,subQ7,subQ8,subQ2]),TDD([makeQuery(id+"F4.boolean.opBoolean","SPLIT",FACE,{"disambiguationData":[TD([makeQuery(id+"F3.opExtrude","SWEPT_FACE",FACE,{"disambiguationData":[OSD([subQ5])]})])],"derivedFrom":subQ14})])],"isStart":false}),makeQuery(id+"F6.opExtrude","CAP_FACE",FACE,{"disambiguationData":[OSD([subQ10,subQ1,subQ13,subQ4,subQ0,subQ5,subQ7,subQ8,subQ2]),TDD([makeQuery(id+"F4.boolean.opBoolean","SPLIT",FACE,{"disambiguationData":[TD([makeQuery(id+"F3.opExtrude","SWEPT_FACE",FACE,{"disambiguationData":[OSD([subQ8])]})])],"derivedFrom":subQ14})])],"isStart":false})]});}
            var sketch = newSketch(context, id + "F11", { "sketchPlane" : qUnion([Q0])});
            skCircle(sketch, "E11.0", {"center": v(0, 0) * mm, "radius": 15 * mm});
            skCircle(sketch, "E12", {"center": v(0, 0) * mm, "radius": 50 * mm});
            skCircle(sketch, "E13", {"center": v(0, 0) * mm, "radius": 38 * mm});
            skPoint(sketch, "E14", {"position": v(-34.76, -15.35) * mm});
            skPoint(sketch, "E15", {"position": v(-45.74, -20.2) * mm});
            skSolve(sketch);
        }
        {
            var Q0;
            {var subQ0=sQuery(id+"F11.wireOp",EDGE,"E12");var subQ1=makeQuery(id+"F6.opExtrude","CAP_EDGE",EDGE,{"disambiguationData":[OSD([sQuery(id+"F0.wireOp",EDGE,"E8.1.0")])],"isStart":false});var subQ2=makeQuery(id+"F11.imprint","INTERSECT",VERTEX,{"derivedFrom":[subQ1,subQ0]});Q0=makeQuery(id+"F11.imprint","IMPRINT",FACE,{"disambiguationData":[TD([[makeQuery(id+"F11.imprint","IMPRINT",EDGE,{"disambiguationData":[TD([[subQ2,-1.0]])],"derivedFrom":subQ0}),1.0]])]});}
            var Q1;
            {var subQ0=sQuery(id+"F11.wireOp",EDGE,"E12");var subQ1=makeQuery(id+"F6.opExtrude","CAP_EDGE",EDGE,{"disambiguationData":[OSD([sQuery(id+"F0.wireOp",EDGE,"E8.1.1")])],"isStart":false});var subQ2=makeQuery(id+"F11.imprint","INTERSECT",VERTEX,{"derivedFrom":[subQ1,subQ0]});Q1=makeQuery(id+"F11.imprint","IMPRINT",FACE,{"disambiguationData":[TD([[makeQuery(id+"F11.imprint","IMPRINT",EDGE,{"disambiguationData":[TD([[subQ2,-1.0]])],"derivedFrom":subQ0}),1.0]])]});}
            var Q2;
            {var subQ0=sQuery(id+"F11.wireOp",EDGE,"E12");var subQ1=makeQuery(id+"F6.opExtrude","CAP_EDGE",EDGE,{"disambiguationData":[OSD([sQuery(id+"F0.wireOp",EDGE,"E8.2.0")])],"isStart":false});var subQ2=makeQuery(id+"F11.imprint","INTERSECT",VERTEX,{"derivedFrom":[subQ1,subQ0]});Q2=makeQuery(id+"F11.imprint","IMPRINT",FACE,{"disambiguationData":[TD([[makeQuery(id+"F11.imprint","IMPRINT",EDGE,{"disambiguationData":[TD([[subQ2,-1.0]])],"derivedFrom":subQ0}),1.0]])]});}
            var Q3;
            {var subQ0=sQuery(id+"F11.wireOp",EDGE,"E12");var subQ1=makeQuery(id+"F6.opExtrude","CAP_EDGE",EDGE,{"disambiguationData":[OSD([sQuery(id+"F0.wireOp",EDGE,"E7.MirrorCS")])],"isStart":false});var subQ2=makeQuery(id+"F11.imprint","INTERSECT",VERTEX,{"derivedFrom":[subQ1,subQ0]});Q3=makeQuery(id+"F11.imprint","IMPRINT",FACE,{"disambiguationData":[TD([[makeQuery(id+"F11.imprint","IMPRINT",EDGE,{"disambiguationData":[TD([[subQ2,1.0]])],"derivedFrom":subQ0}),1.0]])]});}
            var Q4;
            {var subQ0=sQuery(id+"F11.wireOp",EDGE,"E12");var subQ1=makeQuery(id+"F6.opExtrude","CAP_EDGE",EDGE,{"disambiguationData":[OSD([sQuery(id+"F0.wireOp",EDGE,"E6")])],"isStart":false});var subQ2=makeQuery(id+"F11.imprint","INTERSECT",VERTEX,{"derivedFrom":[subQ1,subQ0]});Q4=makeQuery(id+"F11.imprint","IMPRINT",FACE,{"disambiguationData":[TD([[makeQuery(id+"F11.imprint","IMPRINT",EDGE,{"disambiguationData":[TD([[subQ2,1.0]])],"derivedFrom":subQ0}),1.0]])]});}
            var Q5;
            {var subQ0=sQuery(id+"F11.wireOp",EDGE,"E12");var subQ1=makeQuery(id+"F6.opExtrude","CAP_EDGE",EDGE,{"disambiguationData":[OSD([sQuery(id+"F0.wireOp",EDGE,"E6")])],"isStart":false});var subQ2=makeQuery(id+"F11.imprint","INTERSECT",VERTEX,{"derivedFrom":[subQ1,subQ0]});Q5=makeQuery(id+"F11.imprint","IMPRINT",FACE,{"disambiguationData":[TD([[makeQuery(id+"F11.imprint","IMPRINT",EDGE,{"disambiguationData":[TD([[subQ2,-1.0]])],"derivedFrom":subQ0}),1.0]])]});}
            extrude(context, id + "F12", {"entities" : qUnion([Q0, Q1, Q2, Q3, Q4, Q5]), "operationType" : NewBodyOperationType.REMOVE, "oppositeDirection" : true, "depth" : 10 * mm, "offsetDistance" : 25 * mm});
        }
    });
